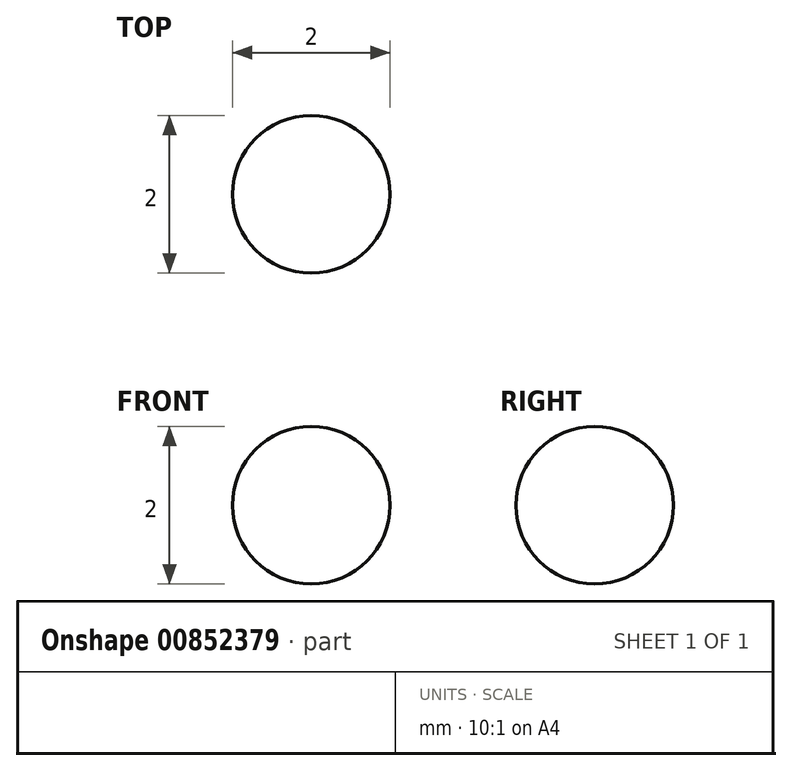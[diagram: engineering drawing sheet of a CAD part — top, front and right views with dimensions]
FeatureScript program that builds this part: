
annotation { "Feature Type Name" : "Feature", "Feature Type Description" : "" }
export const myFeature = defineFeature(function(context is Context, id is Id, definition is map)
    precondition{}
    {
        {
            var Q0;
            Q0=qCreatedBy(makeId("Front.planeOp"),FACE);
            var sketch = newSketch(context, id + "F0", { "sketchPlane" : qUnion([Q0])});
            skFitSpline(sketch, "E0", {"points": [v(0, 3.5) * mm, v(0.52, 2.16) * mm, v(2.13, -0.16) * mm, v(2.9, -1.94) * mm, v(2.4, -2.68) * mm, v(1.67, -3.27) * mm, v(1, -2.8) * mm, v(0, -1.5) * mm, v(-0.22, -2.48) * mm, v(-1.34, -3.23) * mm, v(-1.56, -1.63) * mm, v(-1.94, 0.65) * mm, v(-1.69, 2.1) * mm, v(-1.05, 3.05) * mm, v(0, 3.5) * mm]});
            skCircle(sketch, "E1", {"center": v(0, 0) * mm, "radius": 3.5 * mm, "construction": true});
            skLineSegment(sketch, "E2", {"start": v(-1.34, -3.23) * mm, "end": v(0.22, -3.88) * mm, "construction": true});
            skLineSegment(sketch, "E3", {"start": v(-1.34, -3.23) * mm, "end": v(-1.77, -4.26) * mm, "construction": true});
            skSolve(sketch);
        }
        {
            var Q0;
            Q0=qCreatedBy(makeId("Top.planeOp"),FACE);
            var sketch = newSketch(context, id + "F1", { "sketchPlane" : qUnion([Q0])});
            skLineSegment(sketch, "E4", {"start": v(0, 0) * mm, "end": v(0, -2) * mm, "construction": true});
            skArc(sketch, "E5", {"start": v(0, -1) * mm, "mid": v(1, 0) * mm, "end": v(0, 1) * mm});
            skLineSegment(sketch, "E6", {"start": v(0, 1) * mm, "end": v(0, -1) * mm});
            skSolve(sketch);
        }
        {
            var Q0;
            Q0=makeQuery(id+"F1.imprint","IMPRINT",FACE,{"disambiguationData":[TD([[makeQuery(id+"F1.imprint","IMPRINT",EDGE,{"derivedFrom":sQuery(id+"F1.wireOp",EDGE,"E5")}),1.0]])]});
            var Q1;
            Q1=sQuery(id+"F1.wireOp",EDGE,"E4");
            revolve(context, id + "F2", {"surfaceOperationType" : NewSurfaceOperationType.NEW, "entities" : qUnion([Q0]), "axis" : qUnion([Q1]), "revolveType" : RevolveType.FULL});
        }
        {
            var Q0;
            Q0=sQuery(id+"F0.wireOp",VERTEX,"E2.start");
            var Q1;
            Q1=sQuery(id+"F0.wireOp",EDGE,"E2");
            cPlane(context, id + "F3", {"entities" : qUnion([Q0, Q1]), "cplaneType" : CPlaneType.LINE_POINT, "offset" : 25 * mm, "width" : 150 * mm, "height" : 150 * mm});
        }
    });
